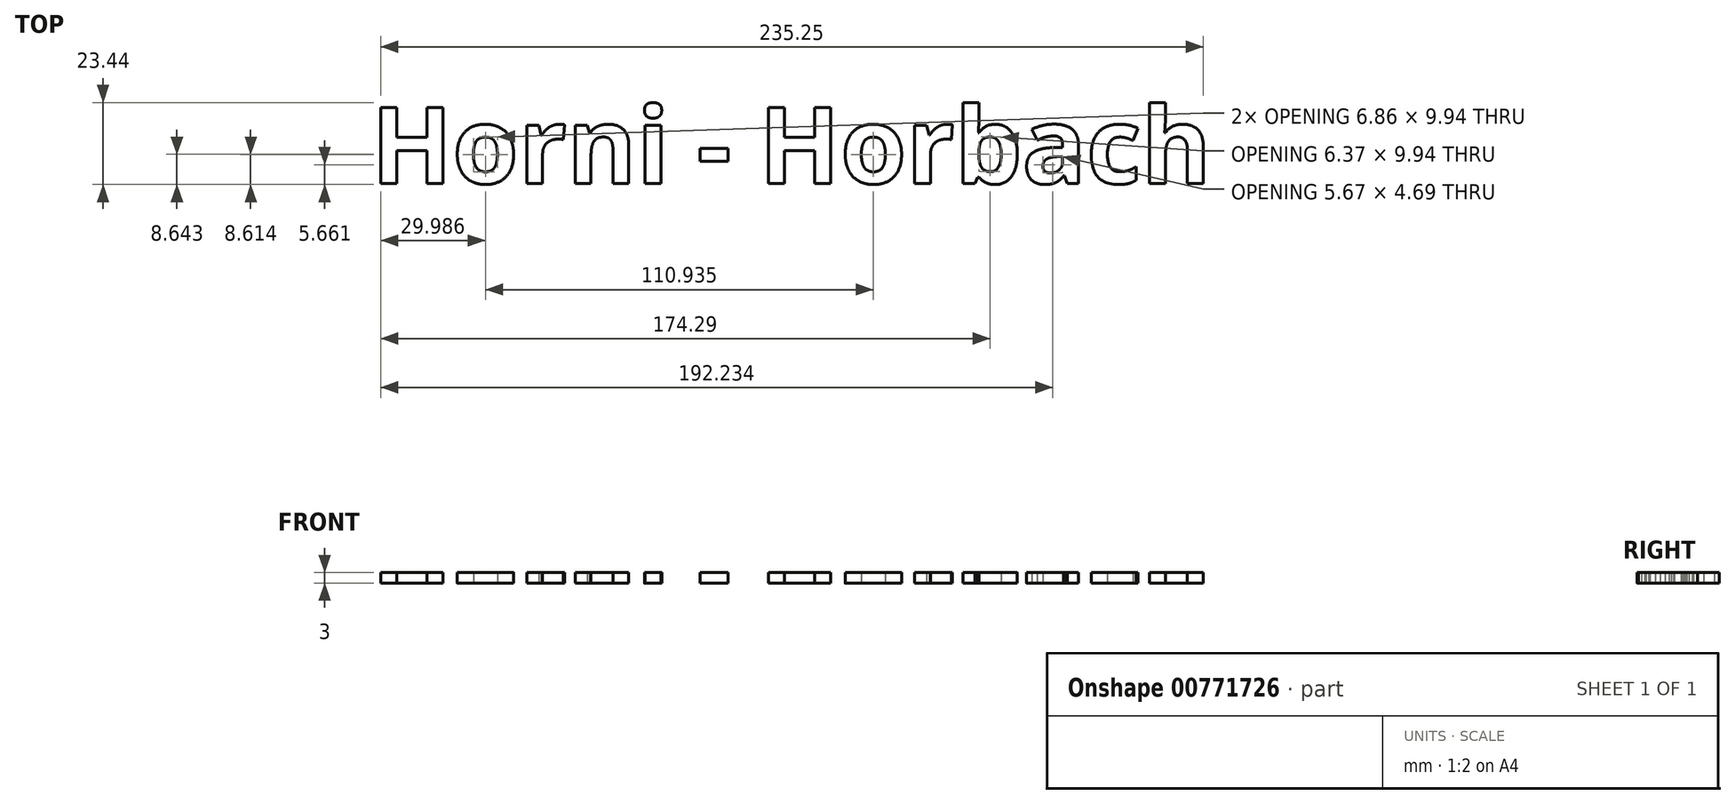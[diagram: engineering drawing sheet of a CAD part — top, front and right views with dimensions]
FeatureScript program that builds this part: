
annotation { "Feature Type Name" : "Feature", "Feature Type Description" : "" }
export const myFeature = defineFeature(function(context is Context, id is Id, definition is map)
    precondition{}
    {
        {
            var Q0;
            Q0=qCreatedBy(makeId("Top.planeOp"),FACE);
            var sketch = newSketch(context, id + "F0", { "sketchPlane" : qUnion([Q0])});
            skText(sketch, "E0", { "text": "Horni - Horbach", "fontName": "OpenSans-Bold.ttf"});
            const initialGuessF0  = {"E0": [0, 0, 1, 0, 0.02193]};
            skSetInitialGuess(sketch, initialGuessF0);
            skSolve(sketch);
        }
        {
            var Q0;
            Q0 = qSketchRegion(id + "F0", true);
            extrude(context, id + "F1", {"entities" : qUnion([Q0]), "depth" : 3 * mm, "offsetDistance" : 25 * mm});
        }
    });
